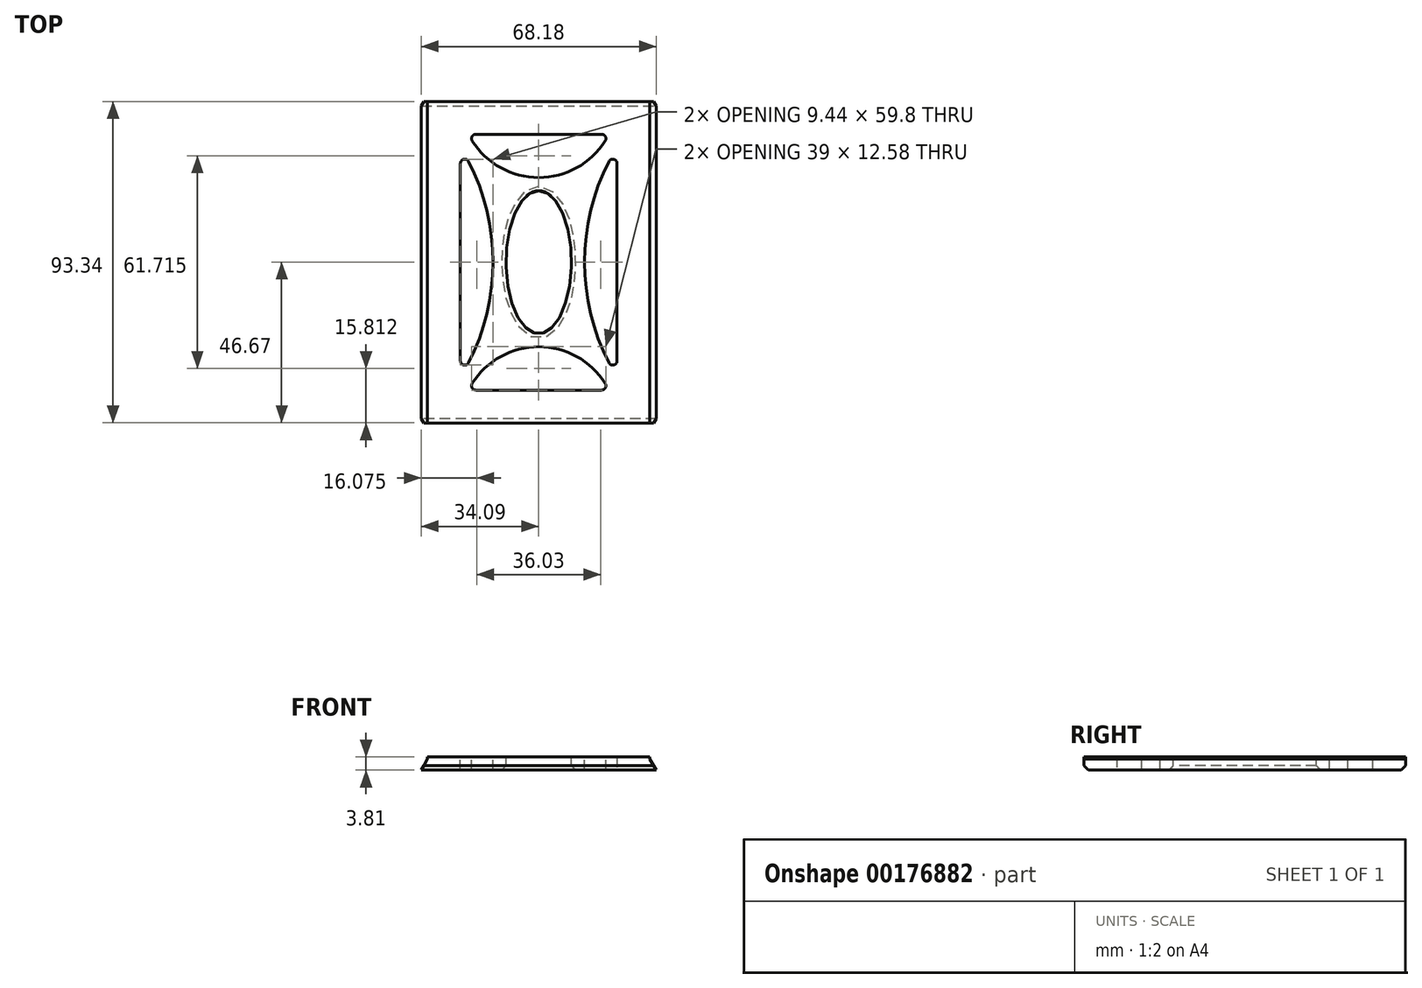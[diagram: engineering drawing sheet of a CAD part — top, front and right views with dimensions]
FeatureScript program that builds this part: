
annotation { "Feature Type Name" : "Feature", "Feature Type Description" : "" }
export const myFeature = defineFeature(function(context is Context, id is Id, definition is map)
    precondition{}
    {
        {
            var Q0;
            Q0=qCreatedBy(makeId("Front.planeOp"),FACE);
            var sketch = newSketch(context, id + "F0", { "sketchPlane" : qUnion([Q0])});
            skLineSegment(sketch, "E0", {"start": v(-34.1, 0) * mm, "end": v(-32.26, 3.17) * mm});
            skLineSegment(sketch, "E1", {"start": v(0, 0) * mm, "end": v(-34.1, 0) * mm});
            skLineSegment(sketch, "E2", {"start": v(-32.26, 3.18) * mm, "end": v(-32.26, 3.81) * mm});
            skLineSegment(sketch, "E3", {"start": v(-32.26, 3.81) * mm, "end": v(0, 3.81) * mm});
            skLineSegment(sketch, "E4", {"start": v(0, 3.81) * mm, "end": v(0, 0) * mm, "construction": true});
            skLineSegment(sketch, "E5.MirrorCS", {"start": v(32.26, 3.8) * mm, "end": v(0, 3.81) * mm});
            skLineSegment(sketch, "E6.MirrorCS", {"start": v(32.26, 3.18) * mm, "end": v(32.26, 3.81) * mm});
            skLineSegment(sketch, "E7.MirrorCS", {"start": v(34.1, 0) * mm, "end": v(32.26, 3.18) * mm});
            skLineSegment(sketch, "E8.MirrorCS", {"start": v(0, 0) * mm, "end": v(34.1, 0) * mm});
            skSolve(sketch);
        }
        {
            var Q0;
            Q0 = qSketchRegion(id + "F0", true);
            extrude(context, id + "F1", {"entities" : qUnion([Q0]), "endBound" : BoundingType.SYMMETRIC, "depth" : 93.34 * mm});
        }
        {
            var Q0;
            Q0=makeQuery(id+"F1.opExtrude","SWEPT_FACE",FACE,{"disambiguationData":[OSD([sQuery(id+"F0.wireOp",EDGE,"E3"),sQuery(id+"F0.wireOp",EDGE,"E5.MirrorCS")])]});
            var sketch = newSketch(context, id + "F2", { "sketchPlane" : qUnion([Q0])});
            skLineSegment(sketch, "E9.top", {"start": v(22.73, -37.15) * mm, "end": v(-22.76, -37.15) * mm, "construction": true});
            skPoint(sketch, "E9.middle", {"position": v(0, 0) * mm});
            skLineSegment(sketch, "E10", {"start": v(22.73, -37.15) * mm, "end": v(-22.73, 37.15) * mm, "construction": true});
            skLineSegment(sketch, "E11", {"start": v(-22.76, -37.15) * mm, "end": v(22.76, 37.15) * mm, "construction": true});
            skArc(sketch, "E12", {"start": v(-22.73, -33.5) * mm, "mid": v(-13.3, 0) * mm, "end": v(-22.73, 33.5) * mm});
            skLineSegment(sketch, "E13", {"start": v(0, 37.15) * mm, "end": v(0, 46.67) * mm, "construction": true});
            skLineSegment(sketch, "E14", {"start": v(-22.73, -33.5) * mm, "end": v(-22.73, 33.5) * mm});
            skLineSegment(sketch, "E15", {"start": v(-32.26, 0) * mm, "end": v(-22.73, 0) * mm, "construction": true});
            skLineSegment(sketch, "E16", {"start": v(-22.73, 33.5) * mm, "end": v(-22.73, 37.15) * mm, "construction": true});
            skLineSegment(sketch, "E17", {"start": v(-22.73, 33.5) * mm, "end": v(-21.1, 34.5) * mm, "construction": true});
            skLineSegment(sketch, "E18", {"start": v(-22.73, 33.5) * mm, "end": v(-1.12, -1.82) * mm, "construction": true});
            skLineSegment(sketch, "E19.MirrorCS", {"start": v(22.73, -33.5) * mm, "end": v(22.73, 33.5) * mm});
            skArc(sketch, "E20.MirrorCS", {"start": v(22.73, -33.5) * mm, "mid": v(13.3, 0) * mm, "end": v(22.73, 33.5) * mm});
            skLineSegment(sketch, "E21.MirrorCS", {"start": v(-19.48, 35.49) * mm, "end": v(-21.1, 34.5) * mm, "construction": true});
            skArc(sketch, "E22", {"start": v(-20.4, 37.15) * mm, "mid": v(0, 24.57) * mm, "end": v(20.4, 37.15) * mm});
            skLineSegment(sketch, "E23", {"start": v(-20.4, 37.15) * mm, "end": v(20.4, 37.15) * mm});
            skLineSegment(sketch, "E24", {"start": v(-19.48, 35.49) * mm, "end": v(1.12, 1.82) * mm, "construction": true});
            skLineSegment(sketch, "E25", {"start": v(-22.73, 37.15) * mm, "end": v(-20.4, 37.15) * mm, "construction": true});
            skLineSegment(sketch, "E26", {"start": v(20.4, 37.15) * mm, "end": v(22.76, 37.15) * mm, "construction": true});
            skLineSegment(sketch, "E27", {"start": v(22.73, 33.5) * mm, "end": v(22.76, 37.15) * mm, "construction": true});
            skLineSegment(sketch, "E28.MirrorCS", {"start": v(-20.4, -37.15) * mm, "end": v(20.4, -37.15) * mm});
            skArc(sketch, "E29.MirrorCS", {"start": v(-20.4, -37.15) * mm, "mid": v(0, -24.57) * mm, "end": v(20.4, -37.15) * mm});
            skLineSegment(sketch, "E30.MirrorCS", {"start": v(22.73, 37.15) * mm, "end": v(-22.76, 37.15) * mm, "construction": true});
            skEllipse(sketch, "E31", {"center": v(0, 0) * mm, "majorRadius": 20.76 * mm, "minorRadius": 9.49 * mm, "majorAxis": v(0, 1)});
            skLineSegment(sketch, "E32", {"start": v(-13.3, 0) * mm, "end": v(-9.49, 0) * mm, "construction": true});
            skLineSegment(sketch, "E33", {"start": v(0, 20.76) * mm, "end": v(0, 24.57) * mm, "construction": true});
            skSolve(sketch);
        }
        {
            var Q0;
            Q0 = qSketchRegion(id + "F2", true);
            extrude(context, id + "F3", {"entities" : qUnion([Q0]), "operationType" : NewBodyOperationType.REMOVE, "endBound" : BoundingType.THROUGH_ALL, "oppositeDirection" : true, "depth" : 25.4 * mm});
        }
        {
            var Q0;
            {var subQ0=sQuery(id+"F2.wireOp",EDGE,"E14");var subQ1=sQuery(id+"F2.wireOp",EDGE,"E12");Q0=makeQuery(id+"F3.boolean.opBoolean","COPY",EDGE,{"derivedFrom":makeQuery(id+"F3.opExtrude","SWEPT_EDGE",EDGE,{"disambiguationData":[OSD([subQ1,subQ0]),TDD([makeQuery(id+"F2.imprint","INTERSECT",VERTEX,{"disambiguationData":[OD(1.0)],"derivedFrom":[subQ1,subQ0]})])]})});}
            var Q1;
            {var subQ0=sQuery(id+"F2.wireOp",EDGE,"E23");var subQ1=sQuery(id+"F2.wireOp",EDGE,"E22");Q1=makeQuery(id+"F3.boolean.opBoolean","COPY",EDGE,{"derivedFrom":makeQuery(id+"F3.opExtrude","SWEPT_EDGE",EDGE,{"disambiguationData":[OSD([subQ1,subQ0]),TDD([makeQuery(id+"F2.imprint","INTERSECT",VERTEX,{"disambiguationData":[OD(0.0)],"derivedFrom":[subQ1,subQ0]})])]})});}
            var Q2;
            {var subQ0=sQuery(id+"F2.wireOp",EDGE,"E23");var subQ1=sQuery(id+"F2.wireOp",EDGE,"E22");Q2=makeQuery(id+"F3.boolean.opBoolean","COPY",EDGE,{"derivedFrom":makeQuery(id+"F3.opExtrude","SWEPT_EDGE",EDGE,{"disambiguationData":[OSD([subQ1,subQ0]),TDD([makeQuery(id+"F2.imprint","INTERSECT",VERTEX,{"disambiguationData":[OD(1.0)],"derivedFrom":[subQ1,subQ0]})])]})});}
            var Q3;
            {var subQ0=sQuery(id+"F2.wireOp",EDGE,"E20.MirrorCS");var subQ1=sQuery(id+"F2.wireOp",EDGE,"E19.MirrorCS");Q3=makeQuery(id+"F3.boolean.opBoolean","COPY",EDGE,{"derivedFrom":makeQuery(id+"F3.opExtrude","SWEPT_EDGE",EDGE,{"disambiguationData":[OSD([subQ1,subQ0]),TDD([makeQuery(id+"F2.imprint","INTERSECT",VERTEX,{"disambiguationData":[OD(1.0)],"derivedFrom":[subQ1,subQ0]})])]})});}
            var Q4;
            {var subQ0=sQuery(id+"F2.wireOp",EDGE,"E14");var subQ1=sQuery(id+"F2.wireOp",EDGE,"E12");Q4=makeQuery(id+"F3.boolean.opBoolean","COPY",EDGE,{"derivedFrom":makeQuery(id+"F3.opExtrude","SWEPT_EDGE",EDGE,{"disambiguationData":[OSD([subQ1,subQ0]),TDD([makeQuery(id+"F2.imprint","INTERSECT",VERTEX,{"disambiguationData":[OD(0.0)],"derivedFrom":[subQ1,subQ0]})])]})});}
            var Q5;
            {var subQ0=sQuery(id+"F2.wireOp",EDGE,"E20.MirrorCS");var subQ1=sQuery(id+"F2.wireOp",EDGE,"E19.MirrorCS");Q5=makeQuery(id+"F3.boolean.opBoolean","COPY",EDGE,{"derivedFrom":makeQuery(id+"F3.opExtrude","SWEPT_EDGE",EDGE,{"disambiguationData":[OSD([subQ1,subQ0]),TDD([makeQuery(id+"F2.imprint","INTERSECT",VERTEX,{"disambiguationData":[OD(0.0)],"derivedFrom":[subQ1,subQ0]})])]})});}
            var Q6;
            {var subQ0=sQuery(id+"F2.wireOp",EDGE,"E29.MirrorCS");var subQ1=sQuery(id+"F2.wireOp",EDGE,"E28.MirrorCS");Q6=makeQuery(id+"F3.boolean.opBoolean","COPY",EDGE,{"derivedFrom":makeQuery(id+"F3.opExtrude","SWEPT_EDGE",EDGE,{"disambiguationData":[OSD([subQ1,subQ0]),TDD([makeQuery(id+"F2.imprint","INTERSECT",VERTEX,{"disambiguationData":[OD(1.0)],"derivedFrom":[subQ1,subQ0]})])]})});}
            var Q7;
            {var subQ0=sQuery(id+"F2.wireOp",EDGE,"E29.MirrorCS");var subQ1=sQuery(id+"F2.wireOp",EDGE,"E28.MirrorCS");Q7=makeQuery(id+"F3.boolean.opBoolean","COPY",EDGE,{"derivedFrom":makeQuery(id+"F3.opExtrude","SWEPT_EDGE",EDGE,{"disambiguationData":[OSD([subQ1,subQ0]),TDD([makeQuery(id+"F2.imprint","INTERSECT",VERTEX,{"disambiguationData":[OD(0.0)],"derivedFrom":[subQ1,subQ0]})])]})});}
            fillet(context, id + "F4", {"entities" : qUnion([Q0, Q1, Q2, Q3, Q4, Q5, Q6, Q7]), "radius" : 1.27 * mm, "tangentPropagation" : true, "allowEdgeOverflow" : false});
        }
        {
            var Q0;
            Q0=makeQuery(id+"F3.boolean.opBoolean","INTERSECT",EDGE,{"derivedFrom":[makeQuery(id+"F1.opExtrude","SWEPT_FACE",FACE,{"disambiguationData":[OSD([sQuery(id+"F0.wireOp",EDGE,"E1"),sQuery(id+"F0.wireOp",EDGE,"E8.MirrorCS")])]}),makeQuery(id+"F3.opExtrude","SWEPT_FACE",FACE,{"disambiguationData":[OSD([sQuery(id+"F2.wireOp",EDGE,"E31")])]})]});
            chamfer(context, id + "F5", {"entities" : qUnion([Q0]), "width" : 1.27 * mm, "tangentPropagation" : true});
        }
        {
            var Q0;
            Q0=makeQuery(id+"F1.opExtrude","CAP_EDGE",EDGE,{"disambiguationData":[OSD([sQuery(id+"F0.wireOp",EDGE,"E1"),sQuery(id+"F0.wireOp",EDGE,"E8.MirrorCS")])],"isStart":true});
            var Q1;
            Q1=makeQuery(id+"F1.opExtrude","CAP_EDGE",EDGE,{"disambiguationData":[OSD([sQuery(id+"F0.wireOp",EDGE,"E1"),sQuery(id+"F0.wireOp",EDGE,"E8.MirrorCS")])],"isStart":false});
            chamfer(context, id + "F6", {"entities" : qUnion([Q0, Q1]), "width" : 1.27 * mm, "tangentPropagation" : true});
        }
    });
